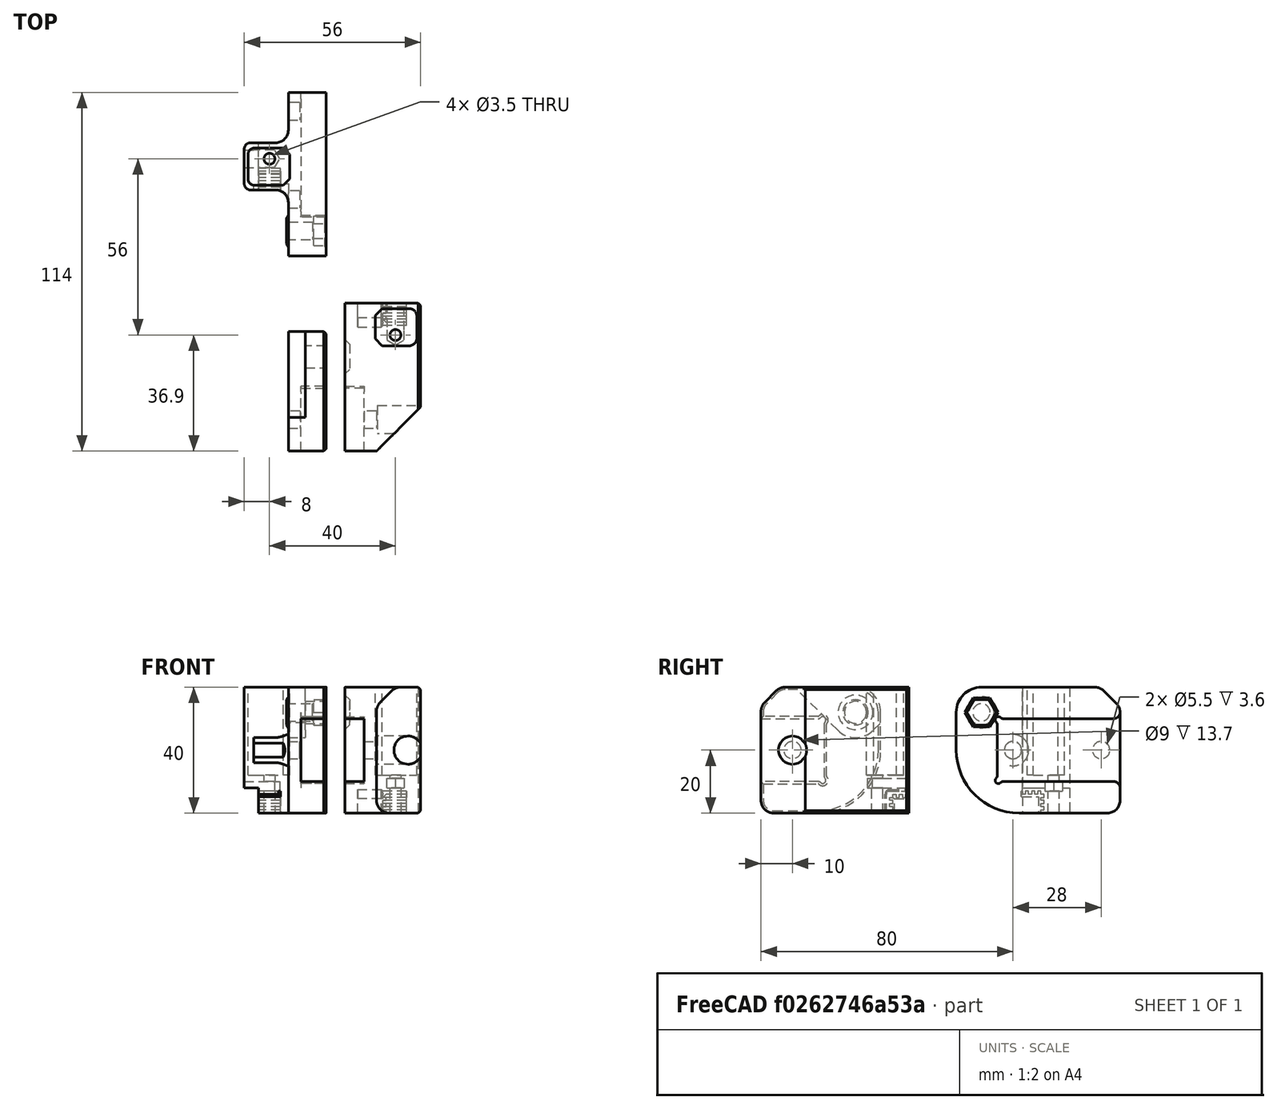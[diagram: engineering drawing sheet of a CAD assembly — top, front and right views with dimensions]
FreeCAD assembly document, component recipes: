
FREECAD ASSEMBLY — COMPONENT RECIPES ("z-carriages")

This assembly document has 2 components, labeled P0..P1 below (a component is one placed body or linked part). 2 of them carry a construction recipe — the FreeCAD feature program that regenerates the part from scratch, quoted from this document or its linked companion documents; the rest are supplied as boundary geometry only. No exploded tour is included for this assembly.
COMPONENT P0 — recipe-attached ("main-front-left", modeled in this document).
Construction recipe (the document's own serialized feature program — sketch geometry with constraints, then the solid features built on it; lengths are millimeters unless a unit is written):

FEATURE [Sketcher::SketchObject] Sketch051
  ArcFitTolerance = 0
  AttachmentOffset = pos=(0,0,6) rot=(0,0,1;0rad)
  AttachmentSupport = -> [YZ_Plane050]
  FullyConstrained = true
  MakeInternals = false
  MapMode = 5
  Placement = pos=(6,0,0) rot=(0.57735,0.57735,0.57735;2.0944rad)
  sketch-geometry (1):
    g0: Circle CenterX=20 CenterY=12 CenterZ=0 NormalX=0 NormalY=0 NormalZ=1 AngleXU=0 Radius=5
  constraints (3):
    c: DistanceY(g0) = 12
    c: DistanceX(g0) = 20
    c: Diameter(g0) = 10
FEATURE [Sketcher::SketchObject] Sketch052
  ArcFitTolerance = 0
  AttachmentOffset = pos=(0,0,5.4) rot=(0,0,1;0rad)
  AttachmentSupport = -> [YZ_Plane050]
  FullyConstrained = true
  MakeInternals = false
  MapMode = 5
  Placement = pos=(5.4,0,0) rot=(0.57735,0.57735,0.57735;2.0944rad)
  expr: .AttachmentOffset.Base.z = Spreadsheet.v_wheel_width / 2
  sketch-geometry (1):
    g0: Circle CenterX=20 CenterY=12 CenterZ=0 NormalX=0 NormalY=0 NormalZ=1 AngleXU=0 Radius=4
  constraints (3):
    c: DistanceY(g0) = 12
    c: DistanceX(g0) = 20
    c: Diameter(g0) = 8
FEATURE [Sketcher::SketchObject] Sketch053
  ArcFitTolerance = 0
  AttachmentOffset = pos=(0,0,13.7) rot=(0,0,1;0rad)
  AttachmentSupport = -> [YZ_Plane050]
  FullyConstrained = true
  MakeInternals = false
  MapMode = 5
  Placement = pos=(13.7,0,0) rot=(0.57735,0.57735,0.57735;2.0944rad)
  sketch-geometry (1):
    g0: Circle CenterX=20 CenterY=12 CenterZ=0 NormalX=0 NormalY=0 NormalZ=1 AngleXU=0 Radius=2.75
  constraints (3):
    c: DistanceY(g0) = 12
    c: DistanceX(g0) = 20
    c: Diameter(g0) = 5.5
FEATURE [Sketcher::SketchObject] Sketch054
  ArcFitTolerance = 0
  AttachmentOffset = pos=(0,0,14) rot=(0,0,1;0rad)
  AttachmentSupport = -> [YZ_Plane050]
  FullyConstrained = true
  MakeInternals = false
  MapMode = 5
  Placement = pos=(14,0,0) rot=(0.57735,0.57735,0.57735;2.0944rad)
  sketch-geometry (7):
    g0: LineSegment StartX=24.7343 StartY=12 StartZ=0 EndX=22.3671 EndY=16.1 EndZ=0
    g1: LineSegment StartX=22.3671 StartY=16.1 StartZ=0 EndX=17.6329 EndY=16.1 EndZ=0
    g2: LineSegment StartX=17.6329 StartY=16.1 StartZ=0 EndX=15.2657 EndY=12 EndZ=0
    g3: LineSegment StartX=15.2657 StartY=12 StartZ=0 EndX=17.6329 EndY=7.9 EndZ=0
    g4: LineSegment StartX=17.6329 StartY=7.9 StartZ=0 EndX=22.3671 EndY=7.9 EndZ=0
    g5: LineSegment StartX=22.3671 StartY=7.9 StartZ=0 EndX=24.7343 EndY=12 EndZ=0
    g6: Circle [constr] CenterX=20 CenterY=12 CenterZ=0 NormalX=0 NormalY=0 NormalZ=1 AngleXU=0 Radius=4.73427
  constraints (17):
    c: Coincident(g0,g1)
    c: Coincident(g1,g2)
    c: Coincident(g2,g3)
    c: Coincident(g3,g4)
    c: Coincident(g4,g5)
    c: Coincident(g5,g0)
    c: Equal(g0, g1-g5) x5
    c: PointOnObject(g0,g6)
    c: PointOnObject(g1,g6)
    c: PointOnObject(g2,g6)
    c: PointOnObject(g3,g6)
    c: PointOnObject(g4,g6)
    c: PointOnObject(g5,g6)
    c: Horizontal(g1)
    c: DistanceY(g4,g0) = 8.2
    c: DistanceY(g6) = 12
    c: DistanceX(g6) = 20
FEATURE [Sketcher::SketchObject] Sketch154
  ArcFitTolerance = 0
  AttachmentSupport = -> [YZ_Plane050]
  FullyConstrained = true
  MakeInternals = false
  MapMode = 5
  Placement = pos=(0,0,0) rot=(0.57735,0.57735,0.57735;2.0944rad)
  sketch-geometry (12):
    g0: ArcOfCircle CenterX=20 CenterY=12 CenterZ=0 NormalX=0 NormalY=0 NormalZ=1 AngleXU=0 Radius=8 StartAngle=1.5708 EndAngle=3.14159
    g1: ArcOfCircle CenterX=32 CenterY=0 CenterZ=0 NormalX=0 NormalY=0 NormalZ=1 AngleXU=0 Radius=20 StartAngle=3.14159 EndAngle=4.71239
    g2: LineSegment StartX=12 StartY=12 StartZ=0 EndX=12 EndY=1.8e-15 EndZ=0
    g3: LineSegment StartX=32 StartY=-20 StartZ=0 EndX=60 EndY=-20 EndZ=0
    g4: LineSegment StartX=64 StartY=12 StartZ=0 EndX=64 EndY=-16 EndZ=0
    g5: ArcOfCircle CenterX=60 CenterY=-16 CenterZ=0 NormalX=0 NormalY=0 NormalZ=1 AngleXU=0 Radius=4 StartAngle=4.71239 EndAngle=6.28319
    g6: GeomPoint [constr] X=64 Y=-20 Z=0
    g7: LineSegment StartX=20 StartY=20 StartZ=0 EndX=56 EndY=20 EndZ=0
    g8: GeomPoint [constr] X=20 Y=20 Z=0
    g9: LineSegment StartX=58.8284 StartY=18.8284 StartZ=0 EndX=62.8284 EndY=14.8284 EndZ=0
    g10: ArcOfCircle CenterX=56 CenterY=16 CenterZ=0 NormalX=0 NormalY=0 NormalZ=1 AngleXU=0 Radius=4 StartAngle=0.785398 EndAngle=1.5708
    g11: ArcOfCircle CenterX=60 CenterY=12 CenterZ=0 NormalX=0 NormalY=0 NormalZ=1 AngleXU=0 Radius=4 StartAngle=0 EndAngle=0.785398
  constraints (29):
    c: Vertical(g2)
    c: Horizontal(g3)
    c: Vertical(g4)
    c: Tangent(g2,g1) = -1.5708
    c: Tangent(g2,g0) = -1.5708
    c: PointOnObject(g6,g3)
    c: PointOnObject(g6,g4)
    c: Tangent(g3,g5) = -1.5708
    c: Tangent(g4,g5) = 1.5708
    c: DistanceX(g6) = 64
    c: Horizontal(g7)
    c: PointOnObject(g8,g0)
    c: Vertical(g8,g0)
    c: Radius(g5) = 4
    c: Tangent(g1,g3) = -1.5708
    c: DistanceY(g1) = -20
    c: DistanceY(g0) = 12
    c: DistanceX(g0) = 20
    c: Radius(g0) = 8
    c: Tangent(g7,g0) = 1.5708
    c: Tangent(g7,g10) = 1.5708
    c: Tangent(g9,g10) = 1.5708
    c: Tangent(g4,g11) = 1.5708
    c: Tangent(g9,g11) = 1.5708
    c: Equal(g11,g10)
    c: Equal(g10,g5)
    c: Angle(g9) = -0.785398
    c: DistanceY(g4) = 12
    c: PointOnObject(g1,g-1)
FEATURE [PartDesign::Pad] Pad046
  Direction = (1,0,0)
  Length = 18
  Length2 = 8
  Placement = pos=(0,0,0) rot=(1,1,1;2.0944rad)
  Profile = -> Sketch154
  ReferenceAxis = -> Sketch154 [N_Axis]
  Suppressed = false
  Type = 4
FEATURE [Sketcher::SketchObject] Sketch155
  ArcFitTolerance = 0
  AttachmentSupport = -> [XY_Plane050]
  FullyConstrained = true
  MakeInternals = false
  MapMode = 5
  sketch-geometry (11):
    g0: LineSegment StartX=6 StartY=10 StartZ=0 EndX=6 EndY=29 EndZ=0
    g1: LineSegment StartX=-10 StartY=33 StartZ=0 EndX=-10 EndY=10 EndZ=0
    g2: LineSegment StartX=-10 StartY=10 StartZ=0 EndX=6 EndY=10 EndZ=0
    g3: ArcOfCircle CenterX=2 CenterY=29 CenterZ=0 NormalX=0 NormalY=0 NormalZ=1 AngleXU=0 Radius=4 StartAngle=1e-16 EndAngle=1.5708
    g4: LineSegment StartX=2 StartY=33 StartZ=0 EndX=-10 EndY=33 EndZ=0
    g5: LineSegment StartX=-10 StartY=48 StartZ=0 EndX=2 EndY=48 EndZ=0
    g6: LineSegment StartX=6 StartY=52 StartZ=0 EndX=6 EndY=64 EndZ=0
    g7: ArcOfCircle CenterX=2 CenterY=52 CenterZ=0 NormalX=0 NormalY=0 NormalZ=1 AngleXU=0 Radius=4 StartAngle=4.71239 EndAngle=6.28319
    g8: GeomPoint [constr] X=6 Y=48 Z=0
    g9: LineSegment StartX=-10 StartY=48 StartZ=0 EndX=-10 EndY=64 EndZ=0
    g10: LineSegment StartX=-10 StartY=64 StartZ=0 EndX=6 EndY=64 EndZ=0
  constraints (30):
    c: Vertical(g0)
    c: Vertical(g1)
    c: Coincident(g1,g2)
    c: Coincident(g2,g0)
    c: Horizontal(g2)
    c: DistanceY(g0) = 10
    c: Coincident(g4,g1)
    c: Tangent(g3,g0) = -1.5708
    c: Tangent(g4,g3) = -1.5708
    c: Radius(g3) = 4
    c: DistanceX(g0) = 6
    c: DistanceY(g1) = 33
    c: DistanceX(g1) = -10
    c: Horizontal(g4)
    c: Horizontal(g5)
    c: Vertical(g6)
    c: DistanceY(g6) = 64
    c: PointOnObject(g8,g5)
    c: PointOnObject(g8,g6)
    c: Tangent(g5,g7) = -1.5708
    c: Tangent(g6,g7) = -1.5708
    c: Equal(g7,g3)
    c: Vertical(g8,g0)
    c: Coincident(g9,g5)
    c: Vertical(g9)
    c: Coincident(g10,g9)
    c: Coincident(g10,g6)
    c: Horizontal(g10)
    c: Vertical(g5,g1)
    c: DistanceY(g1,g5) = 15
FEATURE [PartDesign::Pocket] Pocket084
  BaseFeature = -> Pad046
  Direction = (0,0,-1)
  Length = 5
  Length2 = 5
  Midplane = true
  Placement = pos=(0,0,0) rot=(1,1,1;2.0944rad)
  Profile = -> Sketch155
  ReferenceAxis = -> Sketch155 [N_Axis]
  Suppressed = false
  Type = 1
FEATURE [PartDesign::AdditiveLoft] AdditiveLoft004
  BaseFeature = -> Pocket084
  Closed = false
  Placement = pos=(0,0,0) rot=(1,1,1;2.0944rad)
  Profile = -> Sketch051
  Ruled = false
  Sections = -> [Sketch052]
  Suppressed = false
FEATURE [PartDesign::Pocket] Pocket085
  BaseFeature = -> AdditiveLoft004
  Direction = (-1,0,0)
  Length = 5
  Length2 = 5
  Placement = pos=(0,0,0) rot=(1,1,1;2.0944rad)
  Profile = -> Sketch054
  ReferenceAxis = -> Sketch054 [N_Axis]
  Reversed = true
  Suppressed = false
  Type = 1
FEATURE [PartDesign::Pocket] Pocket086
  BaseFeature = -> Pocket085
  Direction = (-1,0,0)
  Length = 5
  Length2 = 5
  Placement = pos=(0,0,0) rot=(1,1,1;2.0944rad)
  Profile = -> Sketch053
  ReferenceAxis = -> Sketch053 [N_Axis]
  Suppressed = false
  Type = 1
FEATURE [Sketcher::SketchObject] Sketch156
  ArcFitTolerance = 0
  AttachmentOffset = pos=(0,0,10) rot=(0,0,1;0rad)
  AttachmentSupport = -> [YZ_Plane050]
  FullyConstrained = true
  MakeInternals = false
  MapMode = 5
  Placement = pos=(10,0,0) rot=(0.57735,0.57735,0.57735;2.0944rad)
  sketch-geometry (11):
    g0: ArcOfCircle CenterX=25.3536 CenterY=9.64645 CenterZ=0 NormalX=0 NormalY=0 NormalZ=1 AngleXU=0 Radius=1 StartAngle=0.743375 EndAngle=3.96901
    g1: ArcOfCircle CenterX=26.8259 CenterY=11 CenterZ=0 NormalX=0 NormalY=0 NormalZ=1 AngleXU=0 Radius=1 StartAngle=3.88497 EndAngle=4.71239
    g2: ArcOfCircle CenterX=24 CenterY=8.17407 CenterZ=0 NormalX=0 NormalY=0 NormalZ=1 AngleXU=0 Radius=1 StartAngle=-9e-16 EndAngle=0.827421
    g3: LineSegment StartX=62 StartY=10 StartZ=0 EndX=26.8259 EndY=10 EndZ=0
    g4: GeomPoint [constr] X=25 Y=0 Z=0
    g5: LineSegment StartX=25 StartY=8.17407 StartZ=0 EndX=25 EndY=0 EndZ=0
    g6: GeomPoint [constr] X=25 Y=10 Z=0
    g7: LineSegment StartX=64 StartY=12 StartZ=0 EndX=64 EndY=0 EndZ=0
    g8: LineSegment StartX=64 StartY=0 StartZ=0 EndX=25 EndY=0 EndZ=0
    g9: LineSegment [constr] StartX=25 StartY=10 StartZ=0 EndX=25.3536 EndY=9.64645 EndZ=0
    g10: ArcOfCircle CenterX=62 CenterY=12 CenterZ=0 NormalX=0 NormalY=0 NormalZ=1 AngleXU=0 Radius=2 StartAngle=4.71239 EndAngle=6.28319
  constraints (27):
    c: Tangent(g1,g0) = 1.5708
    c: Tangent(g2,g0) = 1.5708
    c: Equal(g2,g0)
    c: Equal(g0,g1)
    c: Radius(g2) = 1
    c: Horizontal(g3)
    c: PointOnObject(g4,g-1)
    c: DistanceX(g4) = 25
    c: Coincident(g5,g4)
    c: Vertical(g5)
    c: Tangent(g5,g2) = 1.5708
    c: PointOnObject(g6,g3)
    c: PointOnObject(g6,g5)
    c: PointOnObject(g7,g-1)
    c: Vertical(g7)
    c: Coincident(g8,g7)
    c: Coincident(g8,g5)
    c: Coincident(g9,g6)
    c: Coincident(g9,g0)
    c: Angle(g9) = -0.785398
    c: Distance(g9) = 0.5
    c: Tangent(g3,g1) = 1.5708
    c: DistanceY(g6) = 10
    c: DistanceX(g7) = 64
    c: Tangent(g10,g3) = 1.5708
    c: Tangent(g10,g7) = 1.5708
    c: Radius(g10) = 2
FEATURE [PartDesign::Pocket] Pocket087
  BaseFeature = -> Pocket086
  Direction = (-1,0,0)
  Length = 5
  Length2 = 5
  Placement = pos=(0,0,0) rot=(1,1,1;2.0944rad)
  Profile = -> Sketch156
  ReferenceAxis = -> Sketch156 [N_Axis]
  Reversed = true
  Suppressed = false
  Type = 1
FEATURE [PartDesign::Mirrored] Mirrored024
  BaseFeature = -> Pocket087
  MirrorPlane = -> XY_Plane050
  Originals = -> [Pocket087]
  Placement = pos=(0,0,0) rot=(1,1,1;2.0944rad)
  Refine = true
  Suppressed = false
  TransformMode = 0
FEATURE [Sketcher::SketchObject] Sketch157
  ArcFitTolerance = 0
  AttachmentOffset = pos=(0,0,3.5) rot=(0,0,1;0rad)
  AttachmentSupport = -> [YZ_Plane050]
  FullyConstrained = true
  MakeInternals = false
  MapMode = 5
  Placement = pos=(3.5,0,0) rot=(0.57735,0.57735,0.57735;2.0944rad)
  sketch-geometry (43):
    g0: LineSegment StartX=38.15 StartY=-20 StartZ=0 EndX=38.9 EndY=-20 EndZ=0
    g1: LineSegment StartX=38.9 StartY=-20 StartZ=0 EndX=38.9 EndY=-19 EndZ=0
    g2: LineSegment StartX=38.9 StartY=-19 StartZ=0 EndX=39.9 EndY=-19 EndZ=0
    g3: LineSegment StartX=39.9 StartY=-19 StartZ=0 EndX=39.9 EndY=-18 EndZ=0
    g4: LineSegment StartX=39.9 StartY=-18 StartZ=0 EndX=38.9 EndY=-18 EndZ=0
    g5: LineSegment StartX=38.9 StartY=-18 StartZ=0 EndX=38.9 EndY=-17 EndZ=0
    g6: LineSegment StartX=38.9 StartY=-17 StartZ=0 EndX=39.9 EndY=-17 EndZ=0
    g7: LineSegment StartX=39.9 StartY=-17 StartZ=0 EndX=39.9 EndY=-16 EndZ=0
    g8: LineSegment StartX=39.9 StartY=-16 StartZ=0 EndX=38.9 EndY=-16 EndZ=0
    g9: LineSegment StartX=38.9 StartY=-16 StartZ=0 EndX=38.9 EndY=-15 EndZ=0
    g10: LineSegment StartX=38.9 StartY=-15 StartZ=0 EndX=39.9 EndY=-15 EndZ=0
    g11: LineSegment StartX=39.9 StartY=-15 StartZ=0 EndX=39.9 EndY=-14 EndZ=0
    g12: LineSegment StartX=39.9 StartY=-14 StartZ=0 EndX=38.9 EndY=-14 EndZ=0
    g13: GeomPoint [constr] X=45 Y=0 Z=0
    g14: GeomPoint [constr] X=38.9 Y=0 Z=0
    g15: GeomPoint [constr] X=38.15 Y=0 Z=0
    g16: LineSegment StartX=38.9 StartY=-14 StartZ=0 EndX=38.9 EndY=-13 EndZ=0
    g17: LineSegment StartX=38.9 StartY=-13 StartZ=0 EndX=37.9 EndY=-13 EndZ=0
    g18: LineSegment StartX=37.9 StartY=-13 StartZ=0 EndX=37.9 EndY=-14 EndZ=0
    g19: LineSegment StartX=37.9 StartY=-14 StartZ=0 EndX=36.9 EndY=-14 EndZ=0
    g20: LineSegment StartX=36.9 StartY=-14 StartZ=0 EndX=36.9 EndY=-13 EndZ=0
    g21: LineSegment StartX=36.9 StartY=-13 StartZ=0 EndX=35.9 EndY=-13 EndZ=0
    g22: LineSegment StartX=35.9 StartY=-13 StartZ=0 EndX=35.9 EndY=-14 EndZ=0
    g23: LineSegment StartX=35.9 StartY=-14 StartZ=0 EndX=34.9 EndY=-14 EndZ=0
    g24: LineSegment StartX=34.9 StartY=-14 StartZ=0 EndX=34.9 EndY=-13 EndZ=0
    g25: LineSegment StartX=34.9 StartY=-13 StartZ=0 EndX=33.9 EndY=-13 EndZ=0
    g26: LineSegment StartX=33.9 StartY=-13 StartZ=0 EndX=33.9 EndY=-14 EndZ=0
    g27: LineSegment StartX=33.9 StartY=-14 StartZ=0 EndX=32.9 EndY=-14 EndZ=0
    g28: LineSegment StartX=32.9 StartY=-14 StartZ=0 EndX=32.9 EndY=-13 EndZ=0
    g29: LineSegment StartX=32.9 StartY=-13 StartZ=0 EndX=31.9 EndY=-13 EndZ=0
    g30: LineSegment StartX=31.9 StartY=-13 StartZ=0 EndX=31.9 EndY=-14 EndZ=0
    g31: LineSegment StartX=31.9 StartY=-14 StartZ=0 EndX=30.9 EndY=-14 EndZ=0
    g32: LineSegment StartX=30.9 StartY=-14 StartZ=0 EndX=30.9 EndY=-13 EndZ=0
    g33: LineSegment StartX=30.9 StartY=-13 StartZ=0 EndX=29.9 EndY=-13 EndZ=0
    g34: LineSegment StartX=29.9 StartY=-13 StartZ=0 EndX=29.9 EndY=-14 EndZ=0
    g35: LineSegment StartX=29.9 StartY=-14 StartZ=0 EndX=28.9 EndY=-14 EndZ=0
    g36: LineSegment StartX=28.9 StartY=-14 StartZ=0 EndX=28.9 EndY=-13 EndZ=0
    g37: LineSegment StartX=28.9 StartY=-13 StartZ=0 EndX=27.9 EndY=-13 EndZ=0
    g38: LineSegment StartX=27.9 StartY=-13 StartZ=0 EndX=27.9 EndY=-14 EndZ=0
    g39: LineSegment StartX=27.9 StartY=-14 StartZ=0 EndX=26.9 EndY=-14 EndZ=0
    g40: LineSegment StartX=26.9 StartY=-14 StartZ=0 EndX=26.9 EndY=-14.75 EndZ=0
    g41: LineSegment StartX=26.9 StartY=-14.75 StartZ=0 EndX=38.15 EndY=-14.75 EndZ=0
    g42: LineSegment StartX=38.15 StartY=-14.75 StartZ=0 EndX=38.15 EndY=-20 EndZ=0
  constraints (126):
    c: Horizontal(g0)
    c: Vertical(g1)
    c: Coincident(g1,g2)
    c: Horizontal(g2)
    c: Coincident(g2,g3)
    c: Vertical(g3)
    c: Coincident(g3,g4)
    c: Horizontal(g4)
    c: Coincident(g4,g5)
    c: Vertical(g5)
    c: Coincident(g5,g6)
    c: Horizontal(g6)
    c: Vertical(g7)
    c: Coincident(g7,g8)
    c: Horizontal(g8)
    c: Coincident(g8,g9)
    c: Vertical(g9)
    c: Coincident(g9,g10)
    c: Horizontal(g10)
    c: Coincident(g10,g11)
    c: Vertical(g11)
    c: Coincident(g11,g12)
    c: Horizontal(g12)
    c: PointOnObject(g13,g-1)
    c: DistanceX(g13) = 45
    c: Vertical(g9,g5)
    c: Vertical(g5,g1)
    c: Vertical(g3,g7)
    c: Vertical(g7,g11)
    c: Equal(g1,g5)
    c: Equal(g5,g9)
    c: Equal(g11,g7)
    c: Equal(g7,g3)
    c: Coincident(g7,g6)
    c: PointOnObject(g14,g-1)
    c: DistanceX(g13,g14) = -6.1
    c: PointOnObject(g15,g-1)
    c: DistanceX(g14,g15) = -0.75
    c: Coincident(g0,g1)
    c: DistanceY(g0) = -20
    c: DistanceY(g1,g1) = 1
    c: DistanceY(g0,g3) = 2
    c: Coincident(g12,g16)
    c: Vertical(g16)
    c: Coincident(g16,g17)
    c: Horizontal(g17)
    c: Coincident(g17,g18)
    c: Vertical(g18)
    c: Coincident(g18,g19)
    c: Horizontal(g19)
    c: Coincident(g19,g20)
    c: Vertical(g20)
    c: Coincident(g20,g21)
    c: Coincident(g21,g22)
    c: Vertical(g22)
    c: Coincident(g22,g23)
    c: Horizontal(g23)
    c: Coincident(g23,g24)
    c: Vertical(g24)
    c: Coincident(g24,g25)
    c: Horizontal(g25)
    c: Coincident(g25,g26)
    c: Vertical(g26)
    c: Coincident(g26,g27)
    c: Horizontal(g27)
    c: Coincident(g27,g28)
    c: Vertical(g28)
    c: Coincident(g28,g29)
    c: Horizontal(g29)
    c: Coincident(g29,g30)
    c: Vertical(g30)
    c: Coincident(g30,g31)
    c: Horizontal(g31)
    c: Coincident(g31,g32)
    c: Vertical(g32)
    c: Coincident(g32,g33)
    c: Horizontal(g33)
    c: Coincident(g33,g34)
    c: Vertical(g34)
    c: Coincident(g34,g35)
    c: Horizontal(g35)
    c: Coincident(g35,g36)
    c: Vertical(g36)
    c: Coincident(g36,g37)
    c: Horizontal(g37)
    c: Coincident(g37,g38)
    c: Vertical(g38)
    c: Coincident(g38,g39)
    c: Horizontal(g39)
    c: Coincident(g39,g40)
    c: Vertical(g40)
    c: Coincident(g40,g41)
    c: Horizontal(g41)
    c: Coincident(g41,g42)
    c: Coincident(g42,g0)
    c: Vertical(g42)
    c: Vertical(g41,g15)
    c: Vertical(g12,g9)
    c: Horizontal(g18,g12)
    c: Horizontal(g12,g22)
    c: Horizontal(g22,g26)
    c: Horizontal(g26,g30)
    c: Horizontal(g30,g34)
    c: Horizontal(g34,g38)
    c: Horizontal(g21)
    c: Horizontal(g17,g21)
    c: Horizontal(g21,g25)
    c: Horizontal(g25,g29)
    c: Horizontal(g29,g33)
    c: Horizontal(g33,g37)
    c: DistanceY(g41,g18) = 0.75
    c: Vertical(g16,g14)
    c: DistanceX(g2,g2) = 1
    c: Equal(g12,g16)
    c: Equal(g17,g11)
    c: Equal(g11,g21)
    c: Equal(g21,g25)
    c: Equal(g25,g29)
    c: Equal(g29,g33)
    c: Equal(g33,g37)
    c: Equal(g39,g35)
    c: Equal(g35,g31)
    c: Equal(g31,g27)
    c: Equal(g27,g23)
    c: Equal(g23,g19)
    c: Equal(g19,g9)
FEATURE [PartDesign::Pocket] Pocket088
  BaseFeature = -> Mirrored024
  Direction = (-1,0,0)
  Length = 5
  Length2 = 5
  Placement = pos=(0,0,0) rot=(1,1,1;2.0944rad)
  Profile = -> Sketch157
  ReferenceAxis = -> Sketch157 [N_Axis]
  Suppressed = false
  Type = 1
FEATURE [Sketcher::SketchObject] Sketch158
  ArcFitTolerance = 0
  AttachmentSupport = -> [XZ_Plane050]
  FullyConstrained = true
  MakeInternals = false
  MapMode = 5
  Placement = pos=(0,0,0) rot=(1,0,0;1.5708rad)
  sketch-geometry (4):
    g0: LineSegment StartX=-8 StartY=-12 StartZ=0 EndX=-3.5 EndY=-12 EndZ=0
    g1: LineSegment StartX=-3.5 StartY=-12 StartZ=0 EndX=-3.5 EndY=-20 EndZ=0
    g2: LineSegment StartX=-8 StartY=-20 StartZ=0 EndX=-8 EndY=-12 EndZ=0
    g3: LineSegment StartX=-3.5 StartY=-20 StartZ=0 EndX=-8 EndY=-20 EndZ=0
  constraints (12):
    c: Coincident(g0,g1)
    c: Coincident(g2,g0)
    c: Horizontal(g0)
    c: Vertical(g1)
    c: Vertical(g2)
    c: DistanceX(g0) = -3.5
    c: DistanceX(g0) = -8
    c: Horizontal(g1,g2)
    c: Coincident(g3,g1)
    c: Coincident(g3,g2)
    c: DistanceY(g1) = -20
    c: DistanceY(g1,g1) = 8
FEATURE [PartDesign::Pocket] Pocket089
  BaseFeature = -> Pocket088
  Direction = (0,1,-2e-16)
  Length = 5
  Length2 = 5
  Midplane = true
  Placement = pos=(0,0,0) rot=(1,1,1;2.0944rad)
  Profile = -> Sketch158
  ReferenceAxis = -> Sketch158 [N_Axis]
  Suppressed = false
  Type = 1
FEATURE [Sketcher::SketchObject] Sketch159
  ArcFitTolerance = 0
  AttachmentOffset = pos=(0,0,-8) rot=(0,0,1;0rad)
  AttachmentSupport = -> [XY_Plane050]
  FullyConstrained = true
  MakeInternals = false
  MapMode = 5
  Placement = pos=(0,0,-8) rot=(0,0,1;0rad)
  sketch-geometry (12):
    g0: GeomPoint [constr] X=0 Y=38.9 Z=0
    g1: GeomPoint [constr] X=0 Y=45 Z=0
    g2: LineSegment StartX=-4.8 StartY=46.3 StartZ=0 EndX=4.4 EndY=46.3 EndZ=0
    g3: LineSegment StartX=6.4 StartY=44.3 StartZ=0 EndX=6.4 EndY=36.5 EndZ=0
    g4: LineSegment StartX=4.4 StartY=34.5 StartZ=0 EndX=-4.8 EndY=34.5 EndZ=0
    g5: LineSegment StartX=-6.8 StartY=36.5 StartZ=0 EndX=-6.8 EndY=44.3 EndZ=0
    g6: ArcOfCircle CenterX=-4.8 CenterY=44.3 CenterZ=0 NormalX=0 NormalY=0 NormalZ=1 AngleXU=0 Radius=2 StartAngle=1.5708 EndAngle=3.14159
    g7: GeomPoint [constr] X=-6.8 Y=46.3 Z=0
    g8: ArcOfCircle CenterX=-4.8 CenterY=36.5 CenterZ=0 NormalX=0 NormalY=0 NormalZ=1 AngleXU=0 Radius=2 StartAngle=3.14159 EndAngle=4.71239
    g9: GeomPoint [constr] X=-6.8 Y=34.5 Z=0
    g10: LineSegment StartX=4.4 StartY=46.3 StartZ=0 EndX=6.4 EndY=44.3 EndZ=0
    g11: LineSegment StartX=6.4 StartY=36.5 StartZ=0 EndX=4.4 EndY=34.5 EndZ=0
  constraints (30):
    c: PointOnObject(g0,g-2)
    c: PointOnObject(g1,g-2)
    c: DistanceY(g1) = 45
    c: DistanceY(g1,g0) = -6.1
    c: Horizontal(g2)
    c: Horizontal(g4)
    c: Vertical(g3)
    c: Vertical(g5)
    c: PointOnObject(g7,g2)
    c: PointOnObject(g7,g5)
    c: Tangent(g2,g6) = 1.5708
    c: Tangent(g5,g6) = 1.5708
    c: PointOnObject(g9,g4)
    c: PointOnObject(g9,g5)
    c: Tangent(g4,g8) = 1.5708
    c: Tangent(g5,g8) = 1.5708
    c: Equal(g6,g8)
    c: Radius(g8) = 2
    c: Coincident(g3,g11)
    c: Coincident(g4,g11)
    c: Coincident(g3,g10)
    c: Coincident(g2,g10)
    c: Perpendicular(g11,g10)
    c: Angle(g11) = -2.35619
    c: Vertical(g4,g2)
    c: DistanceY(g4,g0) = 4.4
    c: DistanceY(g4,g2) = 11.8
    c: DistanceX(g3) = 6.4
    c: Horizontal(g5,g3)
    c: DistanceX(g5) = -6.8
FEATURE [PartDesign::Pocket] Pocket090
  BaseFeature = -> Pocket089
  Direction = (0,0,-1)
  Length = 5
  Length2 = 5
  Placement = pos=(0,0,0) rot=(1,1,1;2.0944rad)
  Profile = -> Sketch159
  ReferenceAxis = -> Sketch159 [N_Axis]
  Reversed = true
  Suppressed = false
  Type = 1
FEATURE [Sketcher::SketchObject] Sketch160
  ArcFitTolerance = 0
  AttachmentSupport = -> [XY_Plane050]
  FullyConstrained = true
  MakeInternals = false
  MapMode = 5
  sketch-geometry (4):
    g0: GeomPoint [constr] X=0 Y=38.9 Z=0
    g1: GeomPoint [constr] X=0 Y=45 Z=0
    g2: GeomPoint [constr] X=0 Y=42.9 Z=0
    g3: Circle CenterX=0 CenterY=42.9 CenterZ=0 NormalX=0 NormalY=0 NormalZ=1 AngleXU=0 Radius=1.75
  constraints (10):
    c: PointOnObject(g0,g-2)
    c: PointOnObject(g1,g-2)
    c: DistanceY(g1) = 45
    c: DistanceY(g1,g0) = -6.1
    c: DistanceY(g2) = 42.9
    c: DistanceY(g1,g2) = -2.1
    c: Coincident(g3,g2)
    c: Diameter(g3) = 3.5
    c: DistanceY(g0,g3) = 4
    c: PointOnObject(g3,g-2)
FEATURE [PartDesign::Pocket] Pocket091
  BaseFeature = -> Pocket090
  Direction = (0,0,-1)
  Length = 5
  Length2 = 5
  Midplane = true
  Placement = pos=(0,0,0) rot=(1,1,1;2.0944rad)
  Profile = -> Sketch160
  ReferenceAxis = -> Sketch160 [N_Axis]
  Suppressed = false
  Type = 1
FEATURE [Sketcher::SketchObject] Sketch161
  ArcFitTolerance = 0
  AttachmentOffset = pos=(0,0,-10) rot=(0,0,1;0rad)
  AttachmentSupport = -> [XY_Plane050]
  FullyConstrained = true
  MakeInternals = false
  MapMode = 5
  Placement = pos=(0,0,-10) rot=(0,0,1;0rad)
  sketch-geometry (13):
    g0: GeomPoint [constr] X=0 Y=42.9 Z=0
    g1: GeomPoint [constr] X=0 Y=38.9 Z=0
    g2: GeomPoint [constr] X=0 Y=45 Z=0
    g3: LineSegment StartX=1.61658 StartY=40.1 StartZ=0 EndX=3.23316 EndY=42.9 EndZ=0
    g4: LineSegment StartX=3.23316 StartY=42.9 StartZ=0 EndX=1.61658 EndY=45.7 EndZ=0
    g5: LineSegment StartX=1.61658 StartY=45.7 StartZ=0 EndX=-1.61658 EndY=45.7 EndZ=0
    g6: LineSegment [constr] StartX=-1.61658 StartY=45.7 StartZ=0 EndX=-3.23316 EndY=42.9 EndZ=0
    g7: LineSegment [constr] StartX=-3.23316 StartY=42.9 StartZ=0 EndX=-1.61658 EndY=40.1 EndZ=0
    g8: LineSegment StartX=-1.61658 StartY=40.1 StartZ=0 EndX=1.61658 EndY=40.1 EndZ=0
    g9: Circle [constr] CenterX=0 CenterY=42.9 CenterZ=0 NormalX=0 NormalY=0 NormalZ=1 AngleXU=0 Radius=3.23316
    g10: LineSegment StartX=-1.61658 StartY=45.7 StartZ=0 EndX=-8 EndY=45.7 EndZ=0
    g11: LineSegment StartX=-1.61658 StartY=40.1 StartZ=0 EndX=-8 EndY=40.1 EndZ=0
    g12: LineSegment StartX=-8 StartY=40.1 StartZ=0 EndX=-8 EndY=45.7 EndZ=0
  constraints (30):
    c: PointOnObject(g0,g-2)
    c: PointOnObject(g1,g-2)
    c: PointOnObject(g2,g-2)
    c: DistanceY(g2) = 45
    c: DistanceY(g2,g1) = -6.1
    c: DistanceY(g1,g0) = 4
    c: Coincident(g3,g4)
    c: Coincident(g4,g5)
    c: Coincident(g5,g6)
    c: Coincident(g6,g7)
    c: Coincident(g7,g8)
    c: Coincident(g8,g3)
    c: Equal(g3, g4-g8) x5
    c: PointOnObject(g3,g9)
    c: PointOnObject(g4,g9)
    c: PointOnObject(g5,g9)
    c: PointOnObject(g6,g9)
    c: PointOnObject(g7,g9)
    c: PointOnObject(g8,g9)
    c: Coincident(g9,g0)
    c: DistanceY(g3,g4) = 5.6
    c: Horizontal(g5)
    c: Coincident(g10,g5)
    c: Horizontal(g10)
    c: Coincident(g11,g8)
    c: Horizontal(g11)
    c: Coincident(g12,g11)
    c: Coincident(g12,g10)
    c: Vertical(g12)
    c: DistanceX(g10) = -8
FEATURE [PartDesign::Pocket] Pocket092
  BaseFeature = -> Pocket091
  Direction = (0,0,-1)
  Length = 3
  Length2 = 5
  Placement = pos=(0,0,0) rot=(1,1,1;2.0944rad)
  Profile = -> Sketch161
  ReferenceAxis = -> Sketch161 [N_Axis]
  Suppressed = false
  Type = 0
FEATURE [Sketcher::SketchObject] Sketch165
  ArcFitTolerance = 0
  AttachmentOffset = pos=(0,0,9.6) rot=(0,0,1;0rad)
  AttachmentSupport = -> [YZ_Plane050]
  FullyConstrained = true
  MakeInternals = false
  MapMode = 5
  Placement = pos=(9.6,0,0) rot=(0.57735,0.57735,0.57735;2.0944rad)
  sketch-geometry (2):
    g0: Circle CenterX=58 CenterY=0 CenterZ=0 NormalX=0 NormalY=0 NormalZ=1 AngleXU=0 Radius=2.75
    g1: Circle CenterX=30 CenterY=0 CenterZ=0 NormalX=0 NormalY=0 NormalZ=1 AngleXU=0 Radius=2.75
  constraints (6):
    c: PointOnObject(g0,g-1)
    c: Diameter(g0) = 5.5
    c: DistanceX(g0) = 58
    c: PointOnObject(g1,g-1)
    c: Diameter(g1) = 5.5
    c: DistanceX(g1) = 30
FEATURE [PartDesign::Pocket] Pocket095
  BaseFeature = -> Pocket092
  Direction = (-1,0,0)
  Length = 5
  Length2 = 5
  Placement = pos=(0,0,0) rot=(1,1,1;2.0944rad)
  Profile = -> Sketch165
  ReferenceAxis = -> Sketch165 [N_Axis]
  Suppressed = false
  Type = 1
FEATURE [Sketcher::SketchObject] Sketch166
  ArcFitTolerance = 0
  AttachmentOffset = pos=(0,0,6) rot=(0,0,1;0rad)
  AttachmentSupport = -> [YZ_Plane050]
  FullyConstrained = true
  MakeInternals = false
  MapMode = 5
  Placement = pos=(6,0,0) rot=(0.57735,0.57735,0.57735;2.0944rad)
  sketch-geometry (1):
    g0: Circle CenterX=30 CenterY=0 CenterZ=0 NormalX=0 NormalY=0 NormalZ=1 AngleXU=0 Radius=5
  constraints (3):
    c: PointOnObject(g0,g-1)
    c: Diameter(g0) = 10
    c: DistanceX(g0) = 30
FEATURE [PartDesign::Pocket] Pocket096
  BaseFeature = -> Pocket095
  Direction = (-1,0,0)
  Length = 11
  Length2 = 5
  Placement = pos=(0,0,0) rot=(1,1,1;2.0944rad)
  Profile = -> Sketch166
  ReferenceAxis = -> Sketch166 [N_Axis]
  Refine = true
  Suppressed = false
  Type = 0
FEATURE [PartDesign::Fillet] Fillet
  Base = -> Pocket096 [Edge121,Edge128]
  BaseFeature = -> Pocket096
  Placement = pos=(0,0,0) rot=(1,1,1;2.0944rad)
  Radius = 2
  SupportTransform = false
  Suppressed = false
  UseAllEdges = false
FEATURE [PartDesign::Chamfer] Chamfer020
  Angle = 45
  Base = -> Fillet [Edge81,Edge79,Edge77,Edge78,Edge80,Edge82]
  BaseFeature = -> Fillet
  ChamferType = 0
  FlipDirection = false
  Placement = pos=(0,0,0) rot=(1,1,1;2.0944rad)
  Size = 0.5
  Size2 = 1
  SupportTransform = false
  Suppressed = false
  UseAllEdges = false
FEATURE [PartDesign::Body] Body050  label="z-carriage-front-left"
  AllowCompound = false
  Group = -> [Sketch051,Sketch052,Sketch053,Sketch054,Sketch154,Pad046,Sketch155,Pocket084,AdditiveLoft004,Pocket085,Pocket086,Sketch156,Pocket087,Mirrored024,Sketch157,Pocket088,Sketch158,Pocket089,Sketch159,Pocket090,Sketch160,Pocket091,Sketch161,Pocket092,Sketch165,Pocket095,Sketch166,Pocket096,Fillet,Chamfer020]
  Origin = -> Origin050
  Tip = -> Chamfer020
COMPONENT P1 — recipe-attached ("main-back-left", modeled in this document).
Construction recipe (the document's own serialized feature program — sketch geometry with constraints, then the solid features built on it; lengths are millimeters unless a unit is written):

FEATURE [Sketcher::SketchObject] Sketch303
  ArcFitTolerance = 0
  AttachmentOffset = pos=(0,0,18) rot=(0,0,1;0rad)
  AttachmentSupport = -> [YZ_Plane294]
  FullyConstrained = true
  MakeInternals = false
  MapMode = 5
  Placement = pos=(18,0,0) rot=(0.57735,0.57735,0.57735;2.0944rad)
  sketch-geometry (12):
    g0: LineSegment StartX=-50 StartY=12.3431 StartZ=0 EndX=-50 EndY=-16 EndZ=0
    g1: LineSegment StartX=-46 StartY=-20 StartZ=0 EndX=-32 EndY=-20 EndZ=0
    g2: LineSegment StartX=-12 StartY=0 StartZ=0 EndX=-12 EndY=12 EndZ=0
    g3: LineSegment StartX=-20 StartY=20 StartZ=0 EndX=-42.3431 EndY=20 EndZ=0
    g4: LineSegment StartX=-45.1716 StartY=18.8284 StartZ=0 EndX=-48.8284 EndY=15.1716 EndZ=0
    g5: ArcOfCircle CenterX=-46 CenterY=12.3431 CenterZ=0 NormalX=0 NormalY=0 NormalZ=1 AngleXU=0 Radius=4 StartAngle=2.35619 EndAngle=3.14159
    g6: ArcOfCircle CenterX=-42.3431 CenterY=16 CenterZ=0 NormalX=0 NormalY=0 NormalZ=1 AngleXU=0 Radius=4 StartAngle=1.5708 EndAngle=2.35619
    g7: ArcOfCircle CenterX=-20 CenterY=12 CenterZ=0 NormalX=0 NormalY=0 NormalZ=1 AngleXU=0 Radius=8 StartAngle=0 EndAngle=1.5708
    g8: ArcOfCircle CenterX=-46 CenterY=-16 CenterZ=0 NormalX=0 NormalY=0 NormalZ=1 AngleXU=0 Radius=4 StartAngle=3.14159 EndAngle=4.71239
    g9: ArcOfCircle CenterX=-32 CenterY=0 CenterZ=0 NormalX=0 NormalY=0 NormalZ=1 AngleXU=0 Radius=20 StartAngle=4.71239 EndAngle=6.28319
    g10: Circle CenterX=-20 CenterY=12 CenterZ=0 NormalX=0 NormalY=0 NormalZ=1 AngleXU=0 Radius=3.5
    g11: GeomPoint X=-50 Y=14 Z=0
  constraints (29):
    c: Vertical(g0)
    c: Horizontal(g1)
    c: Vertical(g2)
    c: Horizontal(g3)
    c: Angle(g4) = -2.35619
    c: Tangent(g0,g5) = -1.5708
    c: Tangent(g4,g5) = -1.5708
    c: Tangent(g3,g6) = -1.5708
    c: Tangent(g4,g6) = -1.5708
    c: Tangent(g2,g7) = -1.5708
    c: Tangent(g3,g7) = -1.5708
    c: Radius(g7) = 8
    c: Equal(g6,g5)
    c: Tangent(g0,g8) = -1.5708
    c: Tangent(g1,g8) = -1.5708
    c: Equal(g8,g5)
    c: Radius(g8) = 4
    c: DistanceY(g1) = -20
    c: DistanceX(g7) = -20
    c: Tangent(g1,g9) = -1.5708
    c: Tangent(g2,g9) = -1.5708
    c: DistanceY(g7) = 12
    c: DistanceX(g0) = -50
    c: Coincident(g10,g7)
    c: Diameter(g10) = 7
    c: PointOnObject(g2,g-1)
    c: PointOnObject(g11,g4)
    c: PointOnObject(g11,g0)
    c: DistanceY(g11) = 14
FEATURE [PartDesign::Pad] Pad074
  Direction = (1,0,0)
  Length = 12
  Length2 = 10
  Placement = pos=(0,0,0) rot=(1,1,1;2.0944rad)
  Profile = -> Sketch303
  ReferenceAxis = -> Sketch303 [N_Axis]
  Reversed = true
  Suppressed = false
  Type = 0
FEATURE [Sketcher::SketchObject] Sketch304
  ArcFitTolerance = 0
  AttachmentOffset = pos=(0,0,10) rot=(0,0,1;0rad)
  AttachmentSupport = -> [YZ_Plane294]
  FullyConstrained = true
  MakeInternals = false
  MapMode = 5
  Placement = pos=(10,0,0) rot=(0.57735,0.57735,0.57735;2.0944rad)
  sketch-geometry (20):
    g0: LineSegment [constr] StartX=-55 StartY=10 StartZ=0 EndX=-30 EndY=10 EndZ=0
    g1: LineSegment [constr] StartX=-30 StartY=10 StartZ=0 EndX=-30 EndY=-10 EndZ=0
    g2: LineSegment [constr] StartX=-30 StartY=-10 StartZ=0 EndX=-55 EndY=-10 EndZ=0
    g3: LineSegment [constr] StartX=-55 StartY=-10 StartZ=0 EndX=-55 EndY=10 EndZ=0
    g4: ArcOfCircle CenterX=-54 CenterY=11 CenterZ=0 NormalX=0 NormalY=0 NormalZ=1 AngleXU=0 Radius=1 StartAngle=3.14159 EndAngle=4.71239
    g5: LineSegment StartX=-55 StartY=11 StartZ=0 EndX=-55 EndY=-11 EndZ=0
    g6: ArcOfCircle CenterX=-54 CenterY=-11 CenterZ=0 NormalX=0 NormalY=0 NormalZ=1 AngleXU=0 Radius=1 StartAngle=1.5708 EndAngle=3.14159
    g7: ArcOfCircle CenterX=-30.4142 CenterY=9.58579 CenterZ=0 NormalX=0 NormalY=0 NormalZ=1 AngleXU=0 Radius=1 StartAngle=5.49779 EndAngle=8.63938
    g8: ArcOfCircle CenterX=-31.8284 CenterY=11 CenterZ=0 NormalX=0 NormalY=0 NormalZ=1 AngleXU=0 Radius=1 StartAngle=4.71239 EndAngle=5.49779
    g9: ArcOfCircle CenterX=-29 CenterY=8.17157 CenterZ=0 NormalX=0 NormalY=0 NormalZ=1 AngleXU=0 Radius=1 StartAngle=2.35619 EndAngle=3.14159
    g10: LineSegment [constr] StartX=-30.4142 StartY=9.58579 StartZ=0 EndX=-30 EndY=10 EndZ=0
    g11: LineSegment [constr] StartX=-29.7071 StartY=8.87868 StartZ=0 EndX=-31.1213 EndY=10.2929 EndZ=0
    g12: LineSegment StartX=-54 StartY=10 StartZ=0 EndX=-31.8284 EndY=10 EndZ=0
    g13: ArcOfCircle CenterX=-30.4142 CenterY=-9.58579 CenterZ=0 NormalX=0 NormalY=0 NormalZ=1 AngleXU=0 Radius=1 StartAngle=3.92699 EndAngle=7.06858
    g14: ArcOfCircle CenterX=-29 CenterY=-8.17157 CenterZ=0 NormalX=0 NormalY=0 NormalZ=1 AngleXU=0 Radius=1 StartAngle=3.14159 EndAngle=3.92699
    g15: ArcOfCircle CenterX=-31.8284 CenterY=-11 CenterZ=0 NormalX=0 NormalY=0 NormalZ=1 AngleXU=0 Radius=1 StartAngle=0.785398 EndAngle=1.5708
    g16: LineSegment [constr] StartX=-31.1213 StartY=-10.2929 StartZ=0 EndX=-29.7071 EndY=-8.87868 EndZ=0
    g17: LineSegment [constr] StartX=-30 StartY=-10 StartZ=0 EndX=-30.4142 EndY=-9.58579 EndZ=0
    g18: LineSegment StartX=-54 StartY=-10 StartZ=0 EndX=-31.8284 EndY=-10 EndZ=0
    g19: LineSegment StartX=-30 StartY=-8.17157 StartZ=0 EndX=-30 EndY=8.17157 EndZ=0
  constraints (52):
    c: Coincident(g0,g1)
    c: Coincident(g1,g2)
    c: Coincident(g2,g3)
    c: Coincident(g3,g0)
    c: Horizontal(g0)
    c: Symmetric(g2,g0,g-1)
    c: DistanceY(g1,g1) = 20
    c: DistanceX(g1) = -30
    c: DistanceX(g2,g2) = 25
    c: Coincident(g5,g4)
    c: Vertical(g5)
    c: Tangent(g5,g4)
    c: PointOnObject(g0,g5)
    c: Tangent(g4,g0) = -1.5708
    c: Tangent(g6,g2) = -1.5708
    c: Tangent(g6,g5) = -1.5708
    c: Equal(g6,g4)
    c: Tangent(g8,g7) = 1.5708
    c: Tangent(g8,g0) = -1.5708
    c: Equal(g8,g7)
    c: Equal(g7,g4)
    c: Tangent(g9,g7) = 1.5708
    c: Tangent(g9,g1) = -1.5708
    c: Coincident(g10,g7)
    c: Coincident(g10,g0)
    c: Angle(g10) = 0.785398
    c: Equal(g7,g9)
    c: Coincident(g11,g7)
    c: Coincident(g11,g7)
    c: PointOnObject(g7,g11)
    c: Radius(g4) = 1
    c: Coincident(g12,g4)
    c: Coincident(g12,g8)
    c: Tangent(g15,g2) = -1.5708
    c: Tangent(g15,g13) = 1.5708
    c: Tangent(g14,g13) = 1.5708
    c: Tangent(g14,g1) = -1.5708
    c: Coincident(g16,g13)
    c: Coincident(g16,g13)
    c: PointOnObject(g13,g16)
    c: Coincident(g17,g1)
    c: Coincident(g17,g13)
    c: Angle(g17) = 2.35619
    c: Equal(g13,g7)
    c: Equal(g14,g13)
    c: Equal(g13,g15)
    c: Coincident(g18,g15)
    c: Horizontal(g18)
    c: Coincident(g19,g14)
    c: Coincident(g19,g9)
    c: Vertical(g19)
    c: Coincident(g18,g6)
FEATURE [PartDesign::Pocket] Pocket191
  BaseFeature = -> Pad074
  Direction = (-1,0,0)
  Length = 5
  Length2 = 5
  Placement = pos=(0,0,0) rot=(1,1,1;2.0944rad)
  Profile = -> Sketch304
  ReferenceAxis = -> Sketch304 [N_Axis]
  Reversed = true
  Suppressed = false
  Type = 1
FEATURE [Sketcher::SketchObject] Sketch305
  ArcFitTolerance = 0
  AttachmentOffset = pos=(0,0,11.4) rot=(0,0,1;0rad)
  AttachmentSupport = -> [YZ_Plane294]
  FullyConstrained = true
  MakeInternals = false
  MapMode = 5
  Placement = pos=(11.4,0,0) rot=(0.57735,0.57735,0.57735;2.0944rad)
  expr: .AttachmentOffset.Base.z = Spreadsheet.v_wheel_width / 2 + 6
  sketch-geometry (8):
    g0: GeomPoint [constr] X=-20 Y=12 Z=0
    g1: GeomPoint [constr] X=-20 Y=2 Z=0
    g2: LineSegment StartX=-25.6569 StartY=6.34315 StartZ=0 EndX=-39.3137 EndY=20 EndZ=0
    g3: LineSegment StartX=-12 StartY=8.68629 StartZ=0 EndX=-12 EndY=20 EndZ=0
    g4: LineSegment StartX=-12 StartY=20 StartZ=0 EndX=-39.3137 EndY=20 EndZ=0
    g5: GeomPoint [constr] X=-20 Y=4 Z=0
    g6: ArcOfCircle CenterX=-20 CenterY=12 CenterZ=0 NormalX=0 NormalY=0 NormalZ=1 AngleXU=0 Radius=8 StartAngle=3.92699 EndAngle=5.49779
    g7: LineSegment StartX=-14.3431 StartY=6.34315 StartZ=0 EndX=-12 EndY=8.68629 EndZ=0
  constraints (19):
    c: DistanceX(g0) = -20
    c: DistanceY(g1) = 2
    c: Vertical(g1,g0)
    c: DistanceX(g3) = -12
    c: Vertical(g3)
    c: Coincident(g4,g3)
    c: Coincident(g4,g2)
    c: Horizontal(g4)
    c: DistanceY(g3) = 20
    c: Coincident(g7,g3)
    c: Tangent(g7,g6) = -1.5708
    c: Angle(g2) = 2.35619
    c: Angle(g7) = 0.785398
    c: Vertical(g5,g6)
    c: DistanceY(g1,g5) = 2
    c: PointOnObject(g5,g6)
    c: Tangent(g6,g2) = 1.5708
    c: Coincident(g0,g6)
    c: DistanceY(g0) = 12
FEATURE [PartDesign::Pocket] Pocket192
  BaseFeature = -> Pocket191
  Direction = (-1,0,0)
  Length = 5
  Length2 = 5
  Placement = pos=(0,0,0) rot=(1,1,1;2.0944rad)
  Profile = -> Sketch305
  ReferenceAxis = -> Sketch305 [N_Axis]
  Suppressed = false
  Type = 1
FEATURE [Sketcher::SketchObject] Sketch306
  ArcFitTolerance = 0
  AttachmentOffset = pos=(0,0,9.7) rot=(0,0,1;0rad)
  AttachmentSupport = -> [YZ_Plane294]
  FullyConstrained = true
  MakeInternals = false
  MapMode = 5
  Placement = pos=(9.7,0,0) rot=(0.57735,0.57735,0.57735;2.0944rad)
  sketch-geometry (3):
    g0: Circle CenterX=-40 CenterY=0 CenterZ=0 NormalX=0 NormalY=0 NormalZ=1 AngleXU=0 Radius=2.75
    g1: GeomPoint [constr] X=-30 Y=0 Z=0
    g2: GeomPoint [constr] X=-50 Y=0 Z=0
  constraints (6):
    c: PointOnObject(g0,g-1)
    c: PointOnObject(g1,g-1)
    c: DistanceX(g1) = -30
    c: DistanceX(g2) = -50
    c: Symmetric(g2,g1,g0)
    c: Diameter(g0) = 5.5
FEATURE [PartDesign::Pocket] Pocket193
  BaseFeature = -> Pocket192
  Direction = (-1,0,0)
  Length = 5
  Length2 = 5
  Placement = pos=(0,0,0) rot=(1,1,1;2.0944rad)
  Profile = -> Sketch306
  ReferenceAxis = -> Sketch306 [N_Axis]
  Suppressed = false
  Type = 1
FEATURE [PartDesign::Chamfer] Chamfer019
  Angle = 45
  Base = -> Pocket193 [Edge26,Edge12]
  BaseFeature = -> Pocket193
  ChamferType = 0
  FlipDirection = false
  Placement = pos=(0,0,0) rot=(1,1,1;2.0944rad)
  Size = 0.75
  Size2 = 1
  SupportTransform = false
  Suppressed = false
  UseAllEdges = false
FEATURE [PartDesign::Body] Body154  label="z-carriage-back-left"
  AllowCompound = false
  Group = -> [Sketch303,Pad074,Sketch304,Pocket191,Sketch305,Pocket192,Sketch306,Pocket193,Chamfer019]
  Origin = -> Origin295
  Tip = -> Chamfer019
FEATURE [Sketcher::SketchObject] Sketch139
  ArcFitTolerance = 0
  AttachmentSupport = -> [YZ_Plane233]
  FullyConstrained = true
  MakeInternals = false
  MapMode = 5
  Placement = pos=(0,0,0) rot=(0.57735,0.57735,0.57735;2.0944rad)
  sketch-geometry (16):
    g0: LineSegment StartX=-30 StartY=8.17157 StartZ=0 EndX=-30 EndY=-8.17157 EndZ=0
    g1: LineSegment StartX=-31.8284 StartY=-10 StartZ=0 EndX=-50 EndY=-10 EndZ=0
    g2: LineSegment StartX=-50 StartY=10 StartZ=0 EndX=-31.8284 EndY=10 EndZ=0
    g3: ArcOfCircle CenterX=-29 CenterY=8.17157 CenterZ=0 NormalX=0 NormalY=0 NormalZ=1 AngleXU=0 Radius=1 StartAngle=2.35619 EndAngle=3.14159
    g4: ArcOfCircle CenterX=-30.4142 CenterY=9.58579 CenterZ=0 NormalX=0 NormalY=0 NormalZ=1 AngleXU=0 Radius=1 StartAngle=5.49779 EndAngle=8.63938
    g5: ArcOfCircle CenterX=-31.8284 CenterY=11 CenterZ=0 NormalX=0 NormalY=0 NormalZ=1 AngleXU=0 Radius=1 StartAngle=4.71239 EndAngle=5.49779
    g6: GeomPoint [constr] X=-30 Y=10 Z=0
    g7: LineSegment [constr] StartX=-30.4142 StartY=9.58579 StartZ=0 EndX=-30 EndY=10 EndZ=0
    g8: LineSegment [constr] StartX=-29.7071 StartY=8.87868 StartZ=0 EndX=-31.1213 EndY=10.2929 EndZ=0
    g9: GeomPoint [constr] X=-30 Y=-10 Z=0
    g10: ArcOfCircle CenterX=-29 CenterY=-8.17157 CenterZ=0 NormalX=0 NormalY=0 NormalZ=1 AngleXU=0 Radius=1 StartAngle=3.14159 EndAngle=3.92699
    g11: ArcOfCircle CenterX=-30.4142 CenterY=-9.58579 CenterZ=0 NormalX=0 NormalY=0 NormalZ=1 AngleXU=0 Radius=1 StartAngle=3.92699 EndAngle=7.06858
    g12: ArcOfCircle CenterX=-31.8284 CenterY=-11 CenterZ=0 NormalX=0 NormalY=0 NormalZ=1 AngleXU=0 Radius=1 StartAngle=0.785398 EndAngle=1.5708
    g13: LineSegment [constr] StartX=-30.4142 StartY=-9.58579 StartZ=0 EndX=-30 EndY=-10 EndZ=0
    g14: LineSegment [constr] StartX=-31.1213 StartY=-10.2929 StartZ=0 EndX=-29.7071 EndY=-8.87868 EndZ=0
    g15: LineSegment StartX=-50 StartY=10 StartZ=0 EndX=-50 EndY=-10 EndZ=0
  constraints (39):
    c: Horizontal(g1)
    c: Horizontal(g2)
    c: Tangent(g3,g0) = -1.5708
    c: Tangent(g4,g3) = 1.5708
    c: Tangent(g5,g4) = 1.5708
    c: Tangent(g5,g2) = -1.5708
    c: Coincident(g7,g4)
    c: Coincident(g7,g6)
    c: Angle(g7) = 0.785398
    c: Equal(g3,g4)
    c: Equal(g4,g5)
    c: Coincident(g8,g3)
    c: Coincident(g8,g4)
    c: PointOnObject(g4,g8)
    c: Radius(g4) = 1
    c: DistanceY(g6) = 10
    c: Tangent(g12,g1) = -1.5708
    c: Tangent(g12,g11) = 1.5708
    c: Tangent(g11,g10) = 1.5708
    c: Tangent(g10,g0) = -1.5708
    c: Equal(g10,g11)
    c: Equal(g11,g12)
    c: Equal(g12,g4)
    c: Coincident(g13,g11)
    c: Coincident(g13,g9)
    c: Perpendicular(g7,g13)
    c: Coincident(g14,g11)
    c: Coincident(g14,g10)
    c: PointOnObject(g11,g14)
    c: Coincident(g15,g2)
    c: Coincident(g15,g1)
    c: Vertical(g15)
    c: Vertical(g0)
    c: Perpendicular(g14,g13)
    c: Symmetric(g9,g6,g-1)
    c: Perpendicular(g8,g7)
    c: PointOnObject(g9,g1)
    c: DistanceX(g0) = -30
    c: DistanceX(g1,g9) = 20
FEATURE [Sketcher::SketchObject] Sketch140
  ArcFitTolerance = 0
  AttachmentSupport = -> [YZ_Plane233]
  FullyConstrained = true
  MakeInternals = false
  MapMode = 5
  Placement = pos=(0,0,0) rot=(0.57735,0.57735,0.57735;2.0944rad)
  sketch-geometry (21):
    g0: GeomPoint [constr] X=-3 Y=0 Z=0
    g1: Circle [constr] CenterX=-3 CenterY=0 CenterZ=0 NormalX=0 NormalY=0 NormalZ=1 AngleXU=0 Radius=6.1
    g2: GeomPoint [constr] X=-9.1 Y=0 Z=0
    g3: LineSegment [constr] StartX=-9.85 StartY=20 StartZ=0 EndX=-8.1 EndY=20 EndZ=0
    g4: LineSegment [constr] StartX=-8.1 StartY=20 StartZ=0 EndX=-8.1 EndY=-20 EndZ=0
    g5: LineSegment [constr] StartX=-8.1 StartY=-20 StartZ=0 EndX=-9.85 EndY=-20 EndZ=0
    g6: LineSegment [constr] StartX=-9.85 StartY=-20 StartZ=0 EndX=-9.85 EndY=20 EndZ=0
    g7: GeomPoint [constr] X=-9.85 Y=0 Z=0
    g8: GeomPoint [constr] X=-8.1 Y=0 Z=0
    g9: LineSegment StartX=-50 StartY=-16 StartZ=0 EndX=-50 EndY=12.3431 EndZ=0
    g10: LineSegment StartX=-48.8284 StartY=15.1716 StartZ=0 EndX=-45.1716 EndY=18.8284 EndZ=0
    g11: LineSegment StartX=-42.3431 StartY=20 StartZ=0 EndX=-3 EndY=20 EndZ=0
    g12: LineSegment StartX=-3 StartY=20 StartZ=0 EndX=-3 EndY=-20 EndZ=0
    g13: LineSegment StartX=-3 StartY=-20 StartZ=0 EndX=-46 EndY=-20 EndZ=0
    g14: ArcOfCircle CenterX=-46 CenterY=-16 CenterZ=0 NormalX=0 NormalY=0 NormalZ=1 AngleXU=0 Radius=4 StartAngle=3.14159 EndAngle=4.71239
    g15: GeomPoint [constr] X=-50 Y=-20 Z=0
    g16: ArcOfCircle CenterX=-46 CenterY=12.3431 CenterZ=0 NormalX=0 NormalY=0 NormalZ=1 AngleXU=0 Radius=4 StartAngle=2.35619 EndAngle=3.14159
    g17: GeomPoint [constr] X=-50 Y=14 Z=0
    g18: ArcOfCircle CenterX=-42.3431 CenterY=16 CenterZ=0 NormalX=0 NormalY=0 NormalZ=1 AngleXU=0 Radius=4 StartAngle=1.5708 EndAngle=2.35619
    g19: GeomPoint [constr] X=-44 Y=20 Z=0
    g20: GeomPoint X=-20 Y=-20 Z=0
  constraints (51):
    c: PointOnObject(g0,g-1)
    c: Coincident(g1,g0)
    c: Diameter(g1) = 12.2
    c: PointOnObject(g2,g1)
    c: PointOnObject(g2,g-1)
    c: Coincident(g3,g4)
    c: Coincident(g4,g5)
    c: Coincident(g5,g6)
    c: Coincident(g6,g3)
    c: Horizontal(g3)
    c: Horizontal(g5)
    c: Vertical(g4)
    c: PointOnObject(g7,g6)
    c: PointOnObject(g8,g4)
    c: PointOnObject(g7,g-1)
    c: PointOnObject(g8,g-1)
    c: DistanceX(g7,g2) = 0.75
    c: DistanceX(g2,g8) = 1
    c: Horizontal(g11)
    c: Coincident(g12,g11)
    c: Coincident(g13,g12)
    c: Horizontal(g13)
    c: DistanceY(g17) = 14
    c: DistanceY(g15) = -20
    c: PointOnObject(g15,g9)
    c: PointOnObject(g15,g13)
    c: Tangent(g9,g14) = 1.5708
    c: Tangent(g13,g14) = 1.5708
    c: Radius(g14) = 4
    c: Vertical(g9)
    c: DistanceY(g19) = 20
    c: Angle(g10) = 0.785398
    c: PointOnObject(g17,g9)
    c: PointOnObject(g17,g10)
    c: Tangent(g9,g16) = 1.5708
    c: Tangent(g10,g16) = 1.5708
    c: PointOnObject(g19,g10)
    c: PointOnObject(g19,g11)
    c: Tangent(g10,g18) = 1.5708
    c: Tangent(g11,g18) = 1.5708
    c: Equal(g18,g16)
    c: Equal(g16,g14)
    c: Vertical(g12)
    c: PointOnObject(g3,g11)
    c: PointOnObject(g5,g13)
    c: Vertical(g6)
    c: PointOnObject(g0,g12)
    c: PointOnObject(g20,g13)
    c: DistanceX(g20,g12) = 17
    c: DistanceX(g15,g20) = 30
    c: DistanceX(g20) = -20
FEATURE [PartDesign::Pad] Pad043
  Direction = (1,0,0)
  Length = 6
  Length2 = 18
  Placement = pos=(0,0,0) rot=(1,1,1;2.0944rad)
  Profile = -> Sketch140
  ReferenceAxis = -> Sketch140 [N_Axis]
  Reversed = true
  Suppressed = false
  Type = 4
FEATURE [PartDesign::Pocket] Pocket072
  BaseFeature = -> Pad043
  Direction = (-1,0,0)
  Length = 5
  Length2 = 5
  Placement = pos=(0,0,0) rot=(1,1,1;2.0944rad)
  Profile = -> Sketch139
  ReferenceAxis = -> Sketch139 [N_Axis]
  Suppressed = false
  Type = 1
FEATURE [Sketcher::SketchObject] Sketch320
  ArcFitTolerance = 0
  AttachmentSupport = -> [XY_Plane233]
  FullyConstrained = true
  MakeInternals = false
  MapMode = 5
  sketch-geometry (3):
    g0: LineSegment StartX=18 StartY=-50 StartZ=0 EndX=18 EndY=-36 EndZ=0
    g1: LineSegment StartX=18 StartY=-36 StartZ=0 EndX=4 EndY=-50 EndZ=0
    g2: LineSegment StartX=4 StartY=-50 StartZ=0 EndX=18 EndY=-50 EndZ=0
  constraints (9):
    c: Vertical(g0)
    c: Coincident(g0,g1)
    c: Coincident(g1,g2)
    c: Coincident(g2,g0)
    c: Horizontal(g2)
    c: Equal(g0,g2)
    c: DistanceX(g0) = 18
    c: DistanceX(g1) = 4
    c: DistanceY(g1) = -50
FEATURE [PartDesign::Pocket] Pocket204
  BaseFeature = -> Pocket072
  Direction = (0,0,-1)
  Length = 5
  Length2 = 5
  Midplane = true
  Placement = pos=(0,0,0) rot=(1,1,1;2.0944rad)
  Profile = -> Sketch320
  ReferenceAxis = -> Sketch320 [N_Axis]
  Suppressed = false
  Type = 1
FEATURE [Sketcher::SketchObject] Sketch321
  ArcFitTolerance = 0
  AttachmentOffset = pos=(0,0,-8) rot=(0,0,1;0rad)
  AttachmentSupport = -> [XY_Plane233]
  FullyConstrained = true
  MakeInternals = false
  MapMode = 5
  Placement = pos=(0,0,-8) rot=(0,0,1;0rad)
  sketch-geometry (21):
    g0: LineSegment StartX=5.83431 StartY=-4.7 StartZ=0 EndX=14.4 EndY=-4.7 EndZ=0
    g1: LineSegment StartX=5.83431 StartY=-16.5 StartZ=0 EndX=14.4 EndY=-16.5 EndZ=0
    g2: LineSegment StartX=16.8 StartY=-14.1 StartZ=0 EndX=16.8 EndY=-7.1 EndZ=0
    g3: LineSegment StartX=5.83431 StartY=-4.7 StartZ=0 EndX=3.6 EndY=-6.93431 EndZ=0
    g4: LineSegment StartX=3.6 StartY=-6.93431 StartZ=0 EndX=3.6 EndY=-14.2657 EndZ=0
    g5: LineSegment StartX=3.6 StartY=-14.2657 StartZ=0 EndX=5.83431 EndY=-16.5 EndZ=0
    g6: LineSegment [constr] StartX=14.4 StartY=-16.1 StartZ=0 EndX=6 EndY=-16.1 EndZ=0
    g7: LineSegment [constr] StartX=6 StartY=-16.1 StartZ=0 EndX=4 EndY=-14.1 EndZ=0
    g8: LineSegment [constr] StartX=4 StartY=-14.1 StartZ=0 EndX=4 EndY=-7.1 EndZ=0
    g9: LineSegment [constr] StartX=4 StartY=-7.1 StartZ=0 EndX=6 EndY=-5.1 EndZ=0
    g10: LineSegment [constr] StartX=6 StartY=-5.1 StartZ=0 EndX=14.4 EndY=-5.1 EndZ=0
    g11: GeomPoint [constr] X=10 Y=-13.1 Z=0
    g12: LineSegment [constr] StartX=16.4 StartY=-14.1 StartZ=0 EndX=16.4 EndY=-7.1 EndZ=0
    g13: ArcOfCircle [constr] CenterX=14.4 CenterY=-7.1 CenterZ=0 NormalX=0 NormalY=0 NormalZ=1 AngleXU=0 Radius=2 StartAngle=2e-16 EndAngle=1.5708
    g14: ArcOfCircle [constr] CenterX=14.4 CenterY=-14.1 CenterZ=0 NormalX=0 NormalY=0 NormalZ=1 AngleXU=0 Radius=2 StartAngle=4.71239 EndAngle=6.28319
    g15: ArcOfCircle CenterX=14.4 CenterY=-14.1 CenterZ=0 NormalX=0 NormalY=0 NormalZ=1 AngleXU=0 Radius=2.4 StartAngle=4.71239 EndAngle=6.28319
    g16: ArcOfCircle CenterX=14.4 CenterY=-7.1 CenterZ=0 NormalX=0 NormalY=0 NormalZ=1 AngleXU=0 Radius=2.4 StartAngle=1e-16 EndAngle=1.5708
    g17: LineSegment [constr] StartX=10.2 StartY=-5.1 StartZ=0 EndX=10.2 EndY=-4.7 EndZ=0
    g18: LineSegment [constr] StartX=3.6 StartY=-10.6 StartZ=0 EndX=4 EndY=-10.6 EndZ=0
    g19: LineSegment [constr] StartX=3.6 StartY=-10.6 StartZ=0 EndX=16.8 EndY=-10.6 EndZ=0
    g20: LineSegment [constr] StartX=5 StartY=-6.1 StartZ=0 EndX=4.71716 EndY=-5.81716 EndZ=0
  constraints (55):
    c: Horizontal(g0)
    c: Horizontal(g1)
    c: Vertical(g2)
    c: Coincident(g3,g0)
    c: Coincident(g4,g3)
    c: Vertical(g4)
    c: Coincident(g5,g1)
    c: Coincident(g5,g4)
    c: Horizontal(g6)
    c: Coincident(g6,g7)
    c: Coincident(g7,g8)
    c: Vertical(g8)
    c: Coincident(g8,g9)
    c: Coincident(g9,g10)
    c: Horizontal(g10)
    c: Vertical(g12)
    c: Tangent(g14,g6) = 1.5708
    c: Tangent(g14,g12) = -1.5708
    c: Tangent(g13,g12) = -1.5708
    c: Tangent(g10,g13) = 1.5708
    c: Angle(g9) = 0.785398
    c: Perpendicular(g9,g7)
    c: Equal(g7,g9)
    c: DistanceY(g6,g9) = 11
    c: Radius(g13) = 2
    c: Equal(g13,g14)
    c: DistanceX(g9,g9) = 2
    c: DistanceX(g11,g12) = 6.4
    c: DistanceY(g6,g11) = 3
    c: DistanceX(g3,g8) = 0.4
    c: Parallel(g3,g9)
    c: Parallel(g5,g7)
    c: Coincident(g15,g14)
    c: Coincident(g16,g13)
    c: Tangent(g0,g16) = 1.5708
    c: Tangent(g16,g2) = -1.5708
    c: Tangent(g15,g2) = -1.5708
    c: Tangent(g15,g1) = -1.5708
    c: PointOnObject(g17,g0)
    c: Vertical(g17)
    c: Symmetric(g9,g10,g17)
    c: Horizontal(g18)
    c: Symmetric(g7,g8,g18)
    c: Equal(g18,g17)
    c: Coincident(g19,g18)
    c: PointOnObject(g19,g2)
    c: Horizontal(g19)
    c: Symmetric(g4,g3,g18)
    c: PointOnObject(g20,g3)
    c: Perpendicular(g9,g20)
    c: Symmetric(g8,g9,g20)
    c: Equal(g20,g18)
    c: DistanceY(g11) = -13.1
    c: DistanceX(g11) = 10
    c: DistanceX(g8,g11) = 6
FEATURE [PartDesign::Pocket] Pocket205
  BaseFeature = -> Pocket204
  Direction = (0,0,-1)
  Length = 5
  Length2 = 5
  Placement = pos=(0,0,0) rot=(1,1,1;2.0944rad)
  Profile = -> Sketch321
  ReferenceAxis = -> Sketch321 [N_Axis]
  Reversed = true
  Suppressed = false
  Type = 1
FEATURE [Sketcher::SketchObject] Sketch322
  ArcFitTolerance = 0
  AttachmentOffset = pos=(-20,0,13.5) rot=(0,0,1;0rad)
  AttachmentSupport = -> [YZ_Plane233]
  FullyConstrained = true
  MakeInternals = false
  MapMode = 5
  Placement = pos=(13.5,-20,0) rot=(0.57735,0.57735,0.57735;2.0944rad)
  sketch-geometry (30):
    g0: GeomPoint [constr] X=10.9 Y=-20 Z=0
    g1: GeomPoint [constr] X=17 Y=0 Z=0
    g2: LineSegment StartX=9.9 StartY=-20 StartZ=0 EndX=10.9 EndY=-20 EndZ=0
    g3: LineSegment StartX=10.9 StartY=-20 StartZ=0 EndX=10.9 EndY=-19 EndZ=0
    g4: LineSegment StartX=10.9 StartY=-19 StartZ=0 EndX=11.9 EndY=-19 EndZ=0
    g5: LineSegment StartX=11.9 StartY=-19 StartZ=0 EndX=11.9 EndY=-18 EndZ=0
    g6: LineSegment StartX=11.9 StartY=-18 StartZ=0 EndX=10.9 EndY=-18 EndZ=0
    g7: LineSegment StartX=10.9 StartY=-18 StartZ=0 EndX=10.9 EndY=-17 EndZ=0
    g8: LineSegment StartX=10.9 StartY=-17 StartZ=0 EndX=11.9 EndY=-17 EndZ=0
    g9: LineSegment StartX=11.9 StartY=-17 StartZ=0 EndX=11.9 EndY=-16 EndZ=0
    g10: LineSegment StartX=11.9 StartY=-16 StartZ=0 EndX=10.9 EndY=-16 EndZ=0
    g11: LineSegment StartX=10.9 StartY=-16 StartZ=0 EndX=10.9 EndY=-15 EndZ=0
    g12: LineSegment StartX=10.9 StartY=-15 StartZ=0 EndX=11.9 EndY=-15 EndZ=0
    g13: LineSegment StartX=11.9 StartY=-15 StartZ=0 EndX=11.9 EndY=-14 EndZ=0
    g14: LineSegment StartX=9.9 StartY=-20 StartZ=0 EndX=9.9 EndY=-13 EndZ=0
    g15: LineSegment StartX=9.9 StartY=-13 StartZ=0 EndX=18.9 EndY=-13 EndZ=0
    g16: LineSegment StartX=11.9 StartY=-14 StartZ=0 EndX=12.9 EndY=-14 EndZ=0
    g17: LineSegment StartX=12.9 StartY=-14 StartZ=0 EndX=12.9 EndY=-15 EndZ=0
    g18: LineSegment StartX=12.9 StartY=-15 StartZ=0 EndX=13.9 EndY=-15 EndZ=0
    g19: LineSegment StartX=13.9 StartY=-15 StartZ=0 EndX=13.9 EndY=-14 EndZ=0
    g20: LineSegment StartX=13.9 StartY=-14 StartZ=0 EndX=14.9 EndY=-14 EndZ=0
    g21: LineSegment StartX=14.9 StartY=-14 StartZ=0 EndX=14.9 EndY=-15 EndZ=0
    g22: LineSegment StartX=14.9 StartY=-15 StartZ=0 EndX=15.9 EndY=-15 EndZ=0
    g23: LineSegment StartX=15.9 StartY=-15 StartZ=0 EndX=15.9 EndY=-14 EndZ=0
    g24: LineSegment StartX=15.9 StartY=-14 StartZ=0 EndX=16.9 EndY=-14 EndZ=0
    g25: LineSegment StartX=16.9 StartY=-14 StartZ=0 EndX=16.9 EndY=-15 EndZ=0
    g26: LineSegment StartX=16.9 StartY=-15 StartZ=0 EndX=17.9 EndY=-15 EndZ=0
    g27: LineSegment StartX=17.9 StartY=-15 StartZ=0 EndX=17.9 EndY=-14 EndZ=0
    g28: LineSegment StartX=17.9 StartY=-14 StartZ=0 EndX=18.9 EndY=-14 EndZ=0
    g29: LineSegment StartX=18.9 StartY=-14 StartZ=0 EndX=18.9 EndY=-13 EndZ=0
  constraints (87):
    c: DistanceY(g2) = -20
    c: PointOnObject(g1,g-1)
    c: DistanceX(g1) = 17
    c: DistanceX(g0,g1) = 6.1
    c: Horizontal(g2,g0)
    c: Coincident(g2,g0)
    c: Coincident(g2,g3)
    c: Coincident(g3,g4)
    c: Horizontal(g4)
    c: Coincident(g4,g5)
    c: Vertical(g5)
    c: Coincident(g5,g6)
    c: Coincident(g6,g7)
    c: Vertical(g7)
    c: Coincident(g7,g8)
    c: Horizontal(g8)
    c: Coincident(g8,g9)
    c: Vertical(g9)
    c: Coincident(g9,g10)
    c: Horizontal(g10)
    c: Coincident(g10,g11)
    c: Vertical(g11)
    c: Coincident(g11,g12)
    c: Horizontal(g12)
    c: Coincident(g12,g13)
    c: Vertical(g13)
    c: Horizontal(g6)
    c: Vertical(g3)
    c: Vertical(g3,g7)
    c: Vertical(g7,g11)
    c: Vertical(g12,g8)
    c: Vertical(g8,g4)
    c: Equal(g3,g5)
    c: Equal(g5,g7)
    c: Equal(g7,g9)
    c: Equal(g9,g11)
    c: Equal(g11,g13)
    c: DistanceY(g2,g5) = 2
    c: DistanceX(g2,g2) = 1
    c: DistanceX(g4,g4) = 1
    c: Coincident(g2,g14)
    c: Vertical(g14)
    c: Coincident(g14,g15)
    c: Horizontal(g15)
    c: Coincident(g13,g16)
    c: Horizontal(g16)
    c: Coincident(g16,g17)
    c: Vertical(g17)
    c: Coincident(g17,g18)
    c: Horizontal(g18)
    c: Coincident(g18,g19)
    c: Vertical(g19)
    c: Coincident(g19,g20)
    c: Horizontal(g20)
    c: Coincident(g20,g21)
    c: Vertical(g21)
    c: Coincident(g21,g22)
    c: Horizontal(g22)
    c: Coincident(g22,g23)
    c: Vertical(g23)
    c: Coincident(g23,g24)
    c: Horizontal(g24)
    c: Coincident(g24,g25)
    c: Vertical(g25)
    c: Coincident(g25,g26)
    c: Horizontal(g26)
    c: Coincident(g26,g27)
    c: Vertical(g27)
    c: Coincident(g27,g28)
    c: Horizontal(g28)
    c: Coincident(g28,g29)
    c: Vertical(g29)
    c: Coincident(g15,g29)
    c: Horizontal(g12,g17)
    c: Horizontal(g17,g21)
    c: Horizontal(g21,g25)
    c: Horizontal(g16,g20)
    c: Horizontal(g20,g24)
    c: Horizontal(g24,g28)
    c: Equal(g18,g22)
    c: Equal(g22,g26)
    c: Equal(g26,g9)
    c: Equal(g24,g28)
    c: Equal(g28,g20)
    c: Equal(g20,g16)
    c: Equal(g16,g11)
    c: Equal(g29,g2)
FEATURE [PartDesign::Pocket] Pocket206
  BaseFeature = -> Pocket205
  Direction = (-1,0,0)
  Length = 8
  Length2 = 5
  Placement = pos=(0,0,0) rot=(1,1,1;2.0944rad)
  Profile = -> Sketch322
  ReferenceAxis = -> Sketch322 [N_Axis]
  Suppressed = false
  Type = 0
FEATURE [Sketcher::SketchObject] Sketch323
  ArcFitTolerance = 0
  AttachmentSupport = -> [XY_Plane233]
  FullyConstrained = true
  MakeInternals = false
  MapMode = 5
  sketch-geometry (1):
    g0: Circle CenterX=10 CenterY=-13.1 CenterZ=0 NormalX=0 NormalY=0 NormalZ=1 AngleXU=0 Radius=1.75
  constraints (3):
    c: Diameter(g0) = 3.5
    c: DistanceX(g0) = 10
    c: DistanceY(g0) = -13.1
FEATURE [PartDesign::Pocket] Pocket207
  BaseFeature = -> Pocket206
  Direction = (0,0,-1)
  Length = 5
  Length2 = 5
  Midplane = true
  Placement = pos=(0,0,0) rot=(1,1,1;2.0944rad)
  Profile = -> Sketch323
  ReferenceAxis = -> Sketch323 [N_Axis]
  Suppressed = false
  Type = 1
FEATURE [Sketcher::SketchObject] Sketch324
  ArcFitTolerance = 0
  AttachmentOffset = pos=(0,0,-9) rot=(0,0,1;0rad)
  AttachmentSupport = -> [XY_Plane233]
  FullyConstrained = true
  MakeInternals = false
  MapMode = 5
  Placement = pos=(0,0,-9) rot=(0,0,1;0rad)
  sketch-geometry (10):
    g0: LineSegment StartX=12.75 StartY=-14.6877 StartZ=0 EndX=12.75 EndY=-11.5123 EndZ=0
    g1: LineSegment [constr] StartX=12.75 StartY=-11.5123 StartZ=0 EndX=10 EndY=-9.92457 EndZ=0
    g2: LineSegment [constr] StartX=10 StartY=-9.92457 StartZ=0 EndX=7.25 EndY=-11.5123 EndZ=0
    g3: LineSegment StartX=7.25 StartY=-11.5123 StartZ=0 EndX=7.25 EndY=-14.6877 EndZ=0
    g4: LineSegment StartX=7.25 StartY=-14.6877 StartZ=0 EndX=10 EndY=-16.2754 EndZ=0
    g5: LineSegment StartX=10 StartY=-16.2754 StartZ=0 EndX=12.75 EndY=-14.6877 EndZ=0
    g6: Circle [constr] CenterX=10 CenterY=-13.1 CenterZ=0 NormalX=0 NormalY=0 NormalZ=1 AngleXU=0 Radius=3.17543
    g7: LineSegment StartX=12.75 StartY=-11.5123 StartZ=0 EndX=12.75 EndY=17 EndZ=0
    g8: LineSegment StartX=12.75 StartY=17 StartZ=0 EndX=7.25 EndY=17 EndZ=0
    g9: LineSegment StartX=7.25 StartY=17 StartZ=0 EndX=7.25 EndY=-11.5123 EndZ=0
  constraints (25):
    c: Coincident(g0,g1)
    c: Coincident(g1,g2)
    c: Coincident(g2,g3)
    c: Coincident(g3,g4)
    c: Coincident(g4,g5)
    c: Coincident(g5,g0)
    c: Equal(g0, g1-g5) x5
    c: PointOnObject(g0,g6)
    c: PointOnObject(g1,g6)
    c: PointOnObject(g2,g6)
    c: PointOnObject(g3,g6)
    c: PointOnObject(g4,g6)
    c: PointOnObject(g5,g6)
    c: DistanceX(g6) = 10
    c: DistanceY(g6) = -13.1
    c: Vertical(g0)
    c: DistanceX(g2,g0) = 5.5
    c: Coincident(g0,g7)
    c: Vertical(g7)
    c: Coincident(g7,g8)
    c: Horizontal(g8)
    c: Coincident(g8,g9)
    c: Coincident(g9,g2)
    c: Vertical(g9)
    c: DistanceY(g7) = 17
FEATURE [PartDesign::Pocket] Pocket208
  BaseFeature = -> Pocket207
  Direction = (0,0,-1)
  Length = 3
  Length2 = 5
  Placement = pos=(0,0,0) rot=(1,1,1;2.0944rad)
  Profile = -> Sketch324
  ReferenceAxis = -> Sketch324 [N_Axis]
  Suppressed = false
  Type = 0
FEATURE [Sketcher::SketchObject] Sketch325
  ArcFitTolerance = 0
  AttachmentOffset = pos=(0,0,4) rot=(0,0,1;0rad)
  AttachmentSupport = -> [YZ_Plane233]
  FullyConstrained = true
  MakeInternals = false
  MapMode = 5
  Placement = pos=(4,0,0) rot=(0.57735,0.57735,0.57735;2.0944rad)
  sketch-geometry (1):
    g0: Circle CenterX=-40 CenterY=0 CenterZ=0 NormalX=0 NormalY=0 NormalZ=1 AngleXU=0 Radius=2.75
  constraints (3):
    c: PointOnObject(g0,g-1)
    c: Diameter(g0) = 5.5
    c: DistanceX(g0) = -40
FEATURE [PartDesign::Pocket] Pocket209
  BaseFeature = -> Pocket208
  Direction = (-1,0,0)
  Length = 5
  Length2 = 5
  Placement = pos=(0,0,0) rot=(1,1,1;2.0944rad)
  Profile = -> Sketch325
  ReferenceAxis = -> Sketch325 [N_Axis]
  Suppressed = false
  Type = 1
FEATURE [Sketcher::SketchObject] Sketch326
  ArcFitTolerance = 0
  AttachmentOffset = pos=(0,0,4.3) rot=(0,0,1;0rad)
  AttachmentSupport = -> [YZ_Plane233]
  FullyConstrained = true
  MakeInternals = false
  MapMode = 5
  Placement = pos=(4.3,0,0) rot=(0.57735,0.57735,0.57735;2.0944rad)
  sketch-geometry (1):
    g0: Circle CenterX=-40 CenterY=0 CenterZ=0 NormalX=0 NormalY=0 NormalZ=1 AngleXU=0 Radius=4.5
  constraints (3):
    c: PointOnObject(g0,g-1)
    c: DistanceX(g0) = -40
    c: Diameter(g0) = 9
FEATURE [PartDesign::Pocket] Pocket210
  BaseFeature = -> Pocket209
  Direction = (-1,0,0)
  Length = 5
  Length2 = 5
  Placement = pos=(0,0,0) rot=(1,1,1;2.0944rad)
  Profile = -> Sketch326
  ReferenceAxis = -> Sketch326 [N_Axis]
  Reversed = true
  Suppressed = false
  Type = 1
FEATURE [Sketcher::SketchObject] Sketch374
  ArcFitTolerance = 0
  AttachmentOffset = pos=(0,-20,12) rot=(0,0,1;0rad)
  AttachmentSupport = -> [XY_Plane233]
  FullyConstrained = true
  MakeInternals = false
  MapMode = 5
  Placement = pos=(0,-20,12) rot=(0,0,1;0rad)
  sketch-geometry (4):
    g0: LineSegment StartX=-4.5 StartY=0 StartZ=0 EndX=-4.5 EndY=4 EndZ=0
    g1: LineSegment StartX=-6 StartY=5.5 StartZ=0 EndX=-6 EndY=0 EndZ=0
    g2: LineSegment StartX=-4.5 StartY=0 StartZ=0 EndX=-6 EndY=0 EndZ=0
    g3: LineSegment StartX=-4.5 StartY=4 StartZ=0 EndX=-6 EndY=5.5 EndZ=0
  constraints (12):
    c: PointOnObject(g0,g-1)
    c: Vertical(g0)
    c: PointOnObject(g1,g-1)
    c: Vertical(g1)
    c: Coincident(g0,g2)
    c: Coincident(g2,g1)
    c: DistanceX(g1) = -6
    c: DistanceY(g0,g0) = 4
    c: Coincident(g3,g0)
    c: Coincident(g3,g1)
    c: Angle(g3) = 2.35619
    c: DistanceX(g3,g3) = 1.5
FEATURE [PartDesign::Groove] Groove017
  Angle = 360
  Angle2 = 60
  Axis = (-1,0,0)
  Base = (-4.5,-20,12)
  BaseFeature = -> Pocket210
  Placement = pos=(0,0,0) rot=(1,1,1;2.0944rad)
  Profile = -> Sketch374
  ReferenceAxis = -> Sketch374 [Edge4]
  Suppressed = false
  Type = 0
FEATURE [Sketcher::SketchObject] Sketch
  ArcFitTolerance = 1e-06
  AttachmentOffset = pos=(0,0,-20) rot=(0,0,1;0rad)
  AttachmentSupport = -> [XY_Plane233]
  FullyConstrained = true
  MakeInternals = false
  MapMode = 5
  Placement = pos=(0,0,-20) rot=(0,0,1;0rad)
  sketch-geometry (6):
    g0: LineSegment StartX=5.5 StartY=-7.6 StartZ=0 EndX=7 EndY=-9.1 EndZ=0
    g1: LineSegment StartX=7 StartY=-9.1 StartZ=0 EndX=5.5 EndY=-10.6 EndZ=0
    g2: GeomPoint X=5.5 Y=-9.1 Z=0
    g3: LineSegment StartX=5.5 StartY=-7.6 StartZ=0 EndX=-2 EndY=-7.6 EndZ=0
    g4: LineSegment StartX=-2 StartY=-7.6 StartZ=0 EndX=-2 EndY=-10.6 EndZ=0
    g5: LineSegment StartX=-2 StartY=-10.6 StartZ=0 EndX=5.5 EndY=-10.6 EndZ=0
  constraints (16):
    c: Coincident(g0,g1)
    c: Symmetric(g1,g0,g2)
    c: Horizontal(g0,g2)
    c: Perpendicular(g1,g0)
    c: DistanceY(g2) = -9.1
    c: DistanceX(g0,g0) = 1.5
    c: Coincident(g0,g3)
    c: Horizontal(g3)
    c: Coincident(g3,g4)
    c: Vertical(g4)
    c: Coincident(g4,g5)
    c: Coincident(g5,g1)
    c: Horizontal(g5)
    c: Vertical(g1,g0)
    c: DistanceX(g4) = -2
    c: DistanceX(g0) = 7
FEATURE [Sketcher::SketchObject] Sketch375
  ArcFitTolerance = 1e-06
  AttachmentOffset = pos=(0,0,-6) rot=(0,0,1;0rad)
  AttachmentSupport = -> [YZ_Plane233]
  FullyConstrained = true
  MakeInternals = false
  MapMode = 5
  Placement = pos=(-6,0,0) rot=(0.57735,0.57735,0.57735;2.0944rad)
  sketch-geometry (3):
    g0: GeomPoint X=-3 Y=-20 Z=0
    g1: LineSegment StartX=-9.1 StartY=-20 StartZ=0 EndX=-9.1 EndY=-14 EndZ=0
    g2: LineSegment StartX=-9.1 StartY=-14 StartZ=0 EndX=-3 EndY=-14 EndZ=0
  constraints (9):
    c: DistanceX(g0) = -3
    c: DistanceY(g0) = -20
    c: Vertical(g1)
    c: Coincident(g1,g2)
    c: Horizontal(g2)
    c: Vertical(g2,g0)
    c: Horizontal(g1,g0)
    c: DistanceY(g1,g1) = 6
    c: DistanceX(g1) = -9.1
FEATURE [PartDesign::SubtractivePipe] SubtractivePipe
  AuxilleryCurvelinear = true
  AuxillerySpineTangent = false
  BaseFeature = -> Groove017
  Binormal = (0,0,0)
  Mode = 0
  Placement = pos=(0,0,0) rot=(1,1,1;2.0944rad)
  Profile = -> Sketch
  Spine = -> Sketch375 [Edge1,Edge2]
  SpineTangent = false
  Suppressed = false
  Transformation = 0
  Transition = 2
FEATURE [PartDesign::Chamfer] Chamfer
  Angle = 45
  Base = -> SubtractivePipe [Edge34,Edge56,Edge5]
  BaseFeature = -> SubtractivePipe
  ChamferType = 0
  FlipDirection = false
  Placement = pos=(0,0,0) rot=(1,1,1;2.0944rad)
  Size = 0.75
  Size2 = 1
  SupportTransform = false
  Suppressed = false
  UseAllEdges = false
FEATURE [PartDesign::Body] Body099  label="z-carriage-belt-mount-left"
  AllowCompound = false
  Group = -> [Sketch139,Sketch140,Pad043,Pocket072,Sketch320,Pocket204,Sketch321,Pocket205,Sketch322,Pocket206,Sketch323,Pocket207,Sketch324,Pocket208,Sketch325,Pocket209,Sketch326,Pocket210,Sketch374,Groove017,Sketch,Sketch375,SubtractivePipe,Chamfer]
  Origin = -> Origin233
  Placement = pos=(30,0,0) rot=(0,0,1;0rad)
  Tip = -> Chamfer
PROVENANCE & LICENSES
A FreeCAD (.FCStd) document from a public repository crawl; recipes are the document's own serialized feature recipes (and, for linked parts, companion documents' recipes).
License: as declared in the source repository (recorded in the dataset sidecar).
